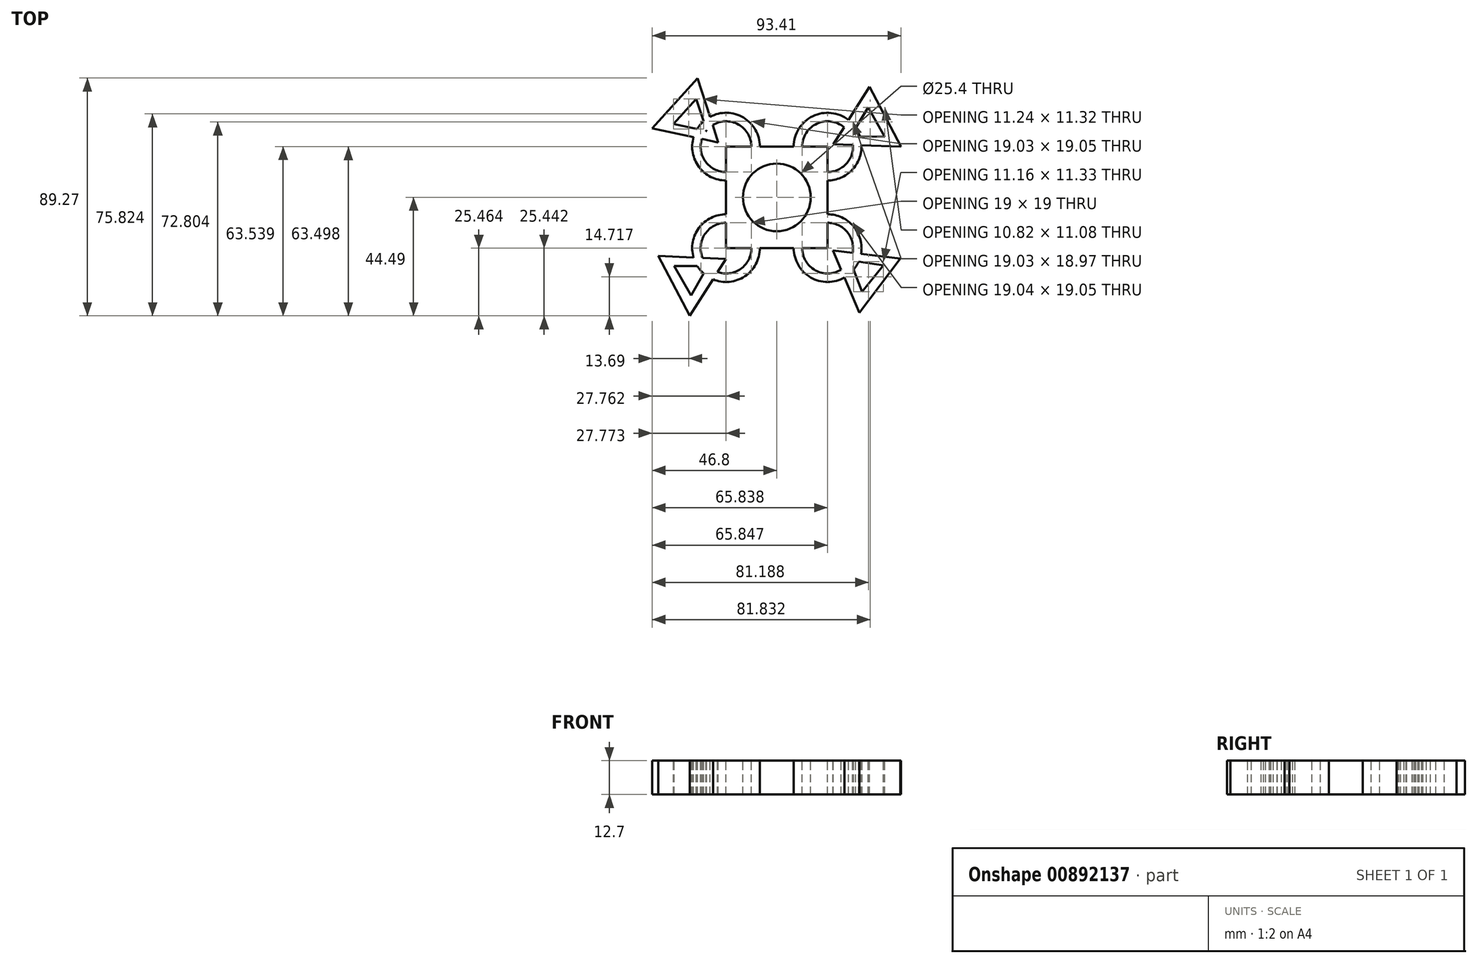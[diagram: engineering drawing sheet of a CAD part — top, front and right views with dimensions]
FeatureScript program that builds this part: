
annotation { "Feature Type Name" : "Feature", "Feature Type Description" : "" }
export const myFeature = defineFeature(function(context is Context, id is Id, definition is map)
    precondition{}
    {
        {
            var Q0;
            Q0=qCreatedBy(makeId("Top.planeOp"),FACE);
            var sketch = newSketch(context, id + "F0", { "sketchPlane" : qUnion([Q0])});
            skLineSegment(sketch, "E0.bottom", {"start": v(19.05, 19.05) * mm, "end": v(-19.05, 19.05) * mm});
            skLineSegment(sketch, "E0.top", {"start": v(19.05, -19.05) * mm, "end": v(-19.05, -19.05) * mm});
            skLineSegment(sketch, "E0.left", {"start": v(19.05, 19.05) * mm, "end": v(19.05, -19.05) * mm});
            skLineSegment(sketch, "E0.right", {"start": v(-19.05, 19.05) * mm, "end": v(-19.05, -19.05) * mm});
            skPoint(sketch, "E0.middle", {"position": v(0, 0) * mm});
            skCircle(sketch, "E1", {"center": v(0, 0) * mm, "radius": 12.7 * mm});
            skSolve(sketch);
        }
        {
            var Q0;
            Q0=makeQuery(id+"F0.imprint","IMPRINT",FACE,{"disambiguationData":[TD([[makeQuery(id+"F0.imprint","IMPRINT",EDGE,{"derivedFrom":sQuery(id+"F0.wireOp",EDGE,"E0.bottom")}),1.0]])]});
            extrude(context, id + "F1", {"entities" : qUnion([Q0]), "endBound" : BoundingType.SYMMETRIC, "oppositeDirection" : true, "depth" : 12.7 * mm, "offsetDistance" : 25.4 * mm});
        }
        {
            var Q0;
            Q0=makeQuery(id+"F1.opExtrude","CAP_FACE",FACE,{"disambiguationData":[OSD([sQuery(id+"F0.wireOp",EDGE,"E0.bottom"),sQuery(id+"F0.wireOp",EDGE,"E0.top"),sQuery(id+"F0.wireOp",EDGE,"E0.left"),sQuery(id+"F0.wireOp",EDGE,"E0.right"),sQuery(id+"F0.wireOp",EDGE,"4GYVzYcs-bTZb-Ygih-5fAQ-AZ7vtdrMuf5R.bottom"),sQuery(id+"F0.wireOp",EDGE,"4GYVzYcs-bTZb-Ygih-5fAQ-AZ7vtdrMuf5R.top"),sQuery(id+"F0.wireOp",EDGE,"4GYVzYcs-bTZb-Ygih-5fAQ-AZ7vtdrMuf5R.left"),sQuery(id+"F0.wireOp",EDGE,"4GYVzYcs-bTZb-Ygih-5fAQ-AZ7vtdrMuf5R.right")])],"isStart":true});
            var sketch = newSketch(context, id + "F2", { "sketchPlane" : qUnion([Q0])});
            skCircle(sketch, "E2", {"center": v(-19.05, 19.05) * mm, "radius": 12.7 * mm});
            skCircle(sketch, "E3", {"center": v(-19.05, 19.05) * mm, "radius": 9.53 * mm});
            skCircle(sketch, "E4", {"center": v(19.05, 19.05) * mm, "radius": 12.7 * mm});
            skCircle(sketch, "E5", {"center": v(19.05, 19.05) * mm, "radius": 9.53 * mm});
            skCircle(sketch, "E6", {"center": v(19.05, -19.05) * mm, "radius": 12.7 * mm});
            skCircle(sketch, "E7", {"center": v(19.05, -19.05) * mm, "radius": 9.53 * mm});
            skCircle(sketch, "E8", {"center": v(-19.05, -19.05) * mm, "radius": 12.7 * mm});
            skCircle(sketch, "E9", {"center": v(-19.05, -19.05) * mm, "radius": 9.53 * mm});
            skSolve(sketch);
        }
        {
            var Q0;
            Q0 = qSketchRegion(id + "F2", true);
            extrude(context, id + "F3", {"entities" : qUnion([Q0]), "operationType" : NewBodyOperationType.ADD, "oppositeDirection" : true, "depth" : 12.7 * mm, "offsetDistance" : 25.4 * mm});
        }
        {
            var Q0;
            Q0=makeQuery(id+"F3.boolean.opBoolean","MERGE",FACE,{"derivedFrom":[makeQuery(id+"F1.opExtrude","CAP_FACE",FACE,{"disambiguationData":[OSD([sQuery(id+"F0.wireOp",EDGE,"E0.bottom"),sQuery(id+"F0.wireOp",EDGE,"E0.top"),sQuery(id+"F0.wireOp",EDGE,"E0.left"),sQuery(id+"F0.wireOp",EDGE,"E0.right"),sQuery(id+"F0.wireOp",EDGE,"4GYVzYcs-bTZb-Ygih-5fAQ-AZ7vtdrMuf5R.bottom"),sQuery(id+"F0.wireOp",EDGE,"4GYVzYcs-bTZb-Ygih-5fAQ-AZ7vtdrMuf5R.top"),sQuery(id+"F0.wireOp",EDGE,"4GYVzYcs-bTZb-Ygih-5fAQ-AZ7vtdrMuf5R.left"),sQuery(id+"F0.wireOp",EDGE,"4GYVzYcs-bTZb-Ygih-5fAQ-AZ7vtdrMuf5R.right")])],"isStart":true}),makeQuery(id+"F3.opExtrude","CAP_FACE",FACE,{"disambiguationData":[OSD([sQuery(id+"F2.wireOp",EDGE,"E2"),sQuery(id+"F2.wireOp",EDGE,"E3")])],"isStart":true}),makeQuery(id+"F3.opExtrude","CAP_FACE",FACE,{"disambiguationData":[OSD([sQuery(id+"F2.wireOp",EDGE,"E4"),sQuery(id+"F2.wireOp",EDGE,"E5")])],"isStart":true}),makeQuery(id+"F3.opExtrude","CAP_FACE",FACE,{"disambiguationData":[OSD([sQuery(id+"F2.wireOp",EDGE,"E6"),sQuery(id+"F2.wireOp",EDGE,"E7")])],"isStart":true}),makeQuery(id+"F3.opExtrude","CAP_FACE",FACE,{"disambiguationData":[OSD([sQuery(id+"F2.wireOp",EDGE,"E8"),sQuery(id+"F2.wireOp",EDGE,"E9")])],"isStart":true})]});
            var sketch = newSketch(context, id + "F4", { "sketchPlane" : qUnion([Q0])});
            skLineSegment(sketch, "E10", {"start": v(21.22, 20) * mm, "end": v(34.74, 41.5) * mm});
            skLineSegment(sketch, "E11", {"start": v(34.74, 41.5) * mm, "end": v(46.6, 19.05) * mm});
            skLineSegment(sketch, "E12", {"start": v(46.6, 19.05) * mm, "end": v(21.22, 20) * mm});
            skLineSegment(sketch, "E13", {"start": v(27.75, 22.94) * mm, "end": v(34.24, 33.85) * mm});
            skLineSegment(sketch, "E14", {"start": v(34.24, 33.85) * mm, "end": v(40.44, 22.77) * mm});
            skLineSegment(sketch, "E15", {"start": v(40.44, 22.77) * mm, "end": v(27.75, 22.94) * mm});
            skLineSegment(sketch, "E16", {"start": v(21.08, -19.9) * mm, "end": v(31, -43.28) * mm});
            skLineSegment(sketch, "E17", {"start": v(31, -43.28) * mm, "end": v(46.29, -23) * mm});
            skLineSegment(sketch, "E18", {"start": v(46.29, -23) * mm, "end": v(21.08, -19.9) * mm});
            skLineSegment(sketch, "E19", {"start": v(27.42, -23.6) * mm, "end": v(32, -35.44) * mm});
            skLineSegment(sketch, "E20", {"start": v(32, -35.44) * mm, "end": v(39.97, -25.55) * mm});
            skLineSegment(sketch, "E21", {"start": v(39.97, -25.55) * mm, "end": v(27.42, -23.6) * mm});
            skLineSegment(sketch, "E22", {"start": v(-19.05, -23.06) * mm, "end": v(-44.43, -21.97) * mm});
            skLineSegment(sketch, "E23", {"start": v(-44.43, -21.97) * mm, "end": v(-32.68, -44.5) * mm});
            skLineSegment(sketch, "E24", {"start": v(-32.68, -44.5) * mm, "end": v(-19.05, -23.06) * mm});
            skLineSegment(sketch, "E25", {"start": v(-25.79, -25.79) * mm, "end": v(-38.49, -25.79) * mm});
            skPoint(sketch, "E25.endSnap0", {"position": v(-25.79, -25.79) * mm});
            skLineSegment(sketch, "E26", {"start": v(-38.49, -25.79) * mm, "end": v(-32.14, -36.78) * mm});
            skLineSegment(sketch, "E27", {"start": v(-32.14, -36.78) * mm, "end": v(-25.79, -25.79) * mm});
            skLineSegment(sketch, "E28", {"start": v(-29.73, 44.78) * mm, "end": v(-46.8, 25.96) * mm});
            skLineSegment(sketch, "E29", {"start": v(-26.32, 24.9) * mm, "end": v(-30.2, 37) * mm});
            skLineSegment(sketch, "E30", {"start": v(-30.2, 37) * mm, "end": v(-38.73, 27.59) * mm});
            skLineSegment(sketch, "E31", {"start": v(-29.73, 44.78) * mm, "end": v(-21.97, 20.6) * mm});
            skLineSegment(sketch, "E32", {"start": v(-21.97, 20.6) * mm, "end": v(-46.8, 25.96) * mm});
            skLineSegment(sketch, "E33", {"start": v(-38.73, 27.59) * mm, "end": v(-26.32, 24.9) * mm});
            skSolve(sketch);
        }
        {
            var Q0;
            Q0 = qSketchRegion(id + "F4", true);
            extrude(context, id + "F5", {"entities" : qUnion([Q0]), "operationType" : NewBodyOperationType.ADD, "oppositeDirection" : true, "depth" : 12.7 * mm, "offsetDistance" : 25.4 * mm});
        }
    });
